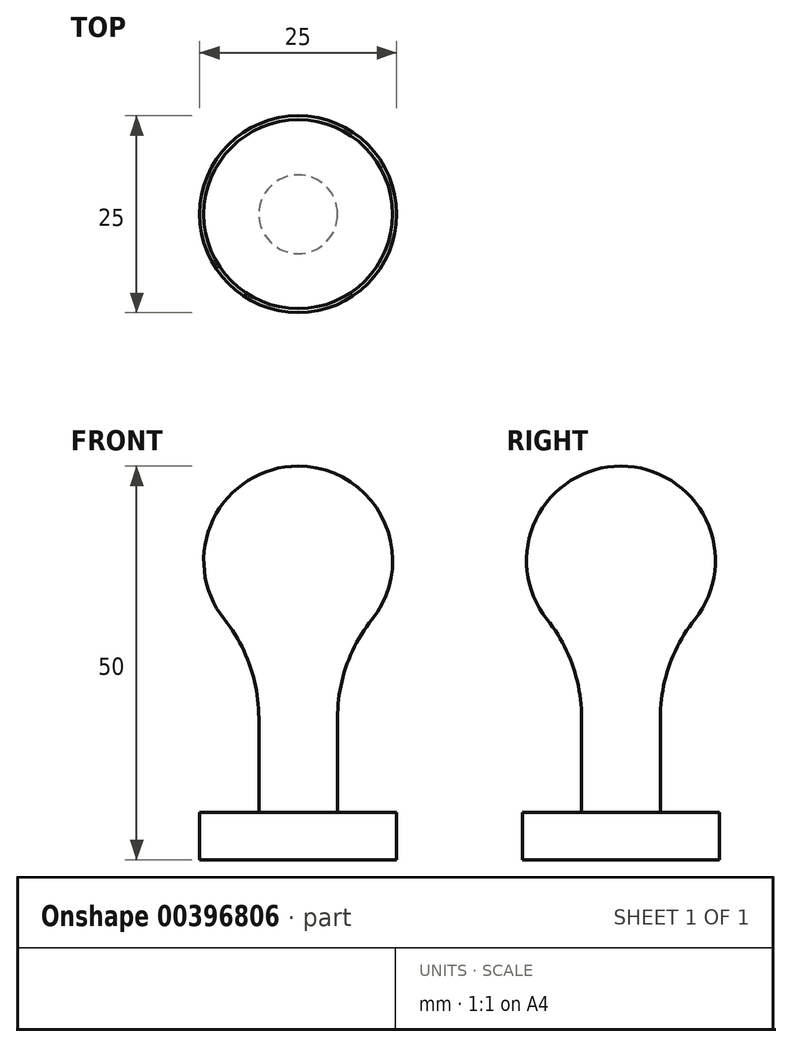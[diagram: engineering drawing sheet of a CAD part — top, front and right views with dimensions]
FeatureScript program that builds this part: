
annotation { "Feature Type Name" : "Feature", "Feature Type Description" : "" }
export const myFeature = defineFeature(function(context is Context, id is Id, definition is map)
    precondition{}
    {
        {
            var Q0;
            Q0=qCreatedBy(makeId("Front.planeOp"),FACE);
            var sketch = newSketch(context, id + "F0", { "sketchPlane" : qUnion([Q0])});
            skLineSegment(sketch, "E0", {"start": v(5, 18) * mm, "end": v(5, 6) * mm});
            skLineSegment(sketch, "E1", {"start": v(5, 6) * mm, "end": v(12.5, 6) * mm});
            skLineSegment(sketch, "E2", {"start": v(12.5, 6) * mm, "end": v(12.5, 0) * mm});
            skLineSegment(sketch, "E3", {"start": v(12.5, 0) * mm, "end": v(0, 0) * mm});
            skLineSegment(sketch, "E4", {"start": v(0, 0) * mm, "end": v(0, 50) * mm});
            skArc(sketch, "E5", {"start": v(9.38, 30.52) * mm, "mid": v(10.81, 43.2) * mm, "end": v(0, 50) * mm});
            skArc(sketch, "E6", {"start": v(5, 18) * mm, "mid": v(6.13, 24.63) * mm, "end": v(9.38, 30.52) * mm});
            skSolve(sketch);
        }
        {
            var Q0;
            Q0 = qSketchRegion(id + "F0", true);
            var Q1;
            Q1=sQuery(id+"F0.wireOp",EDGE,"E4");
            revolve(context, id + "F1", {"entities" : qUnion([Q0]), "axis" : qUnion([Q1]), "revolveType" : RevolveType.FULL});
        }
    });
